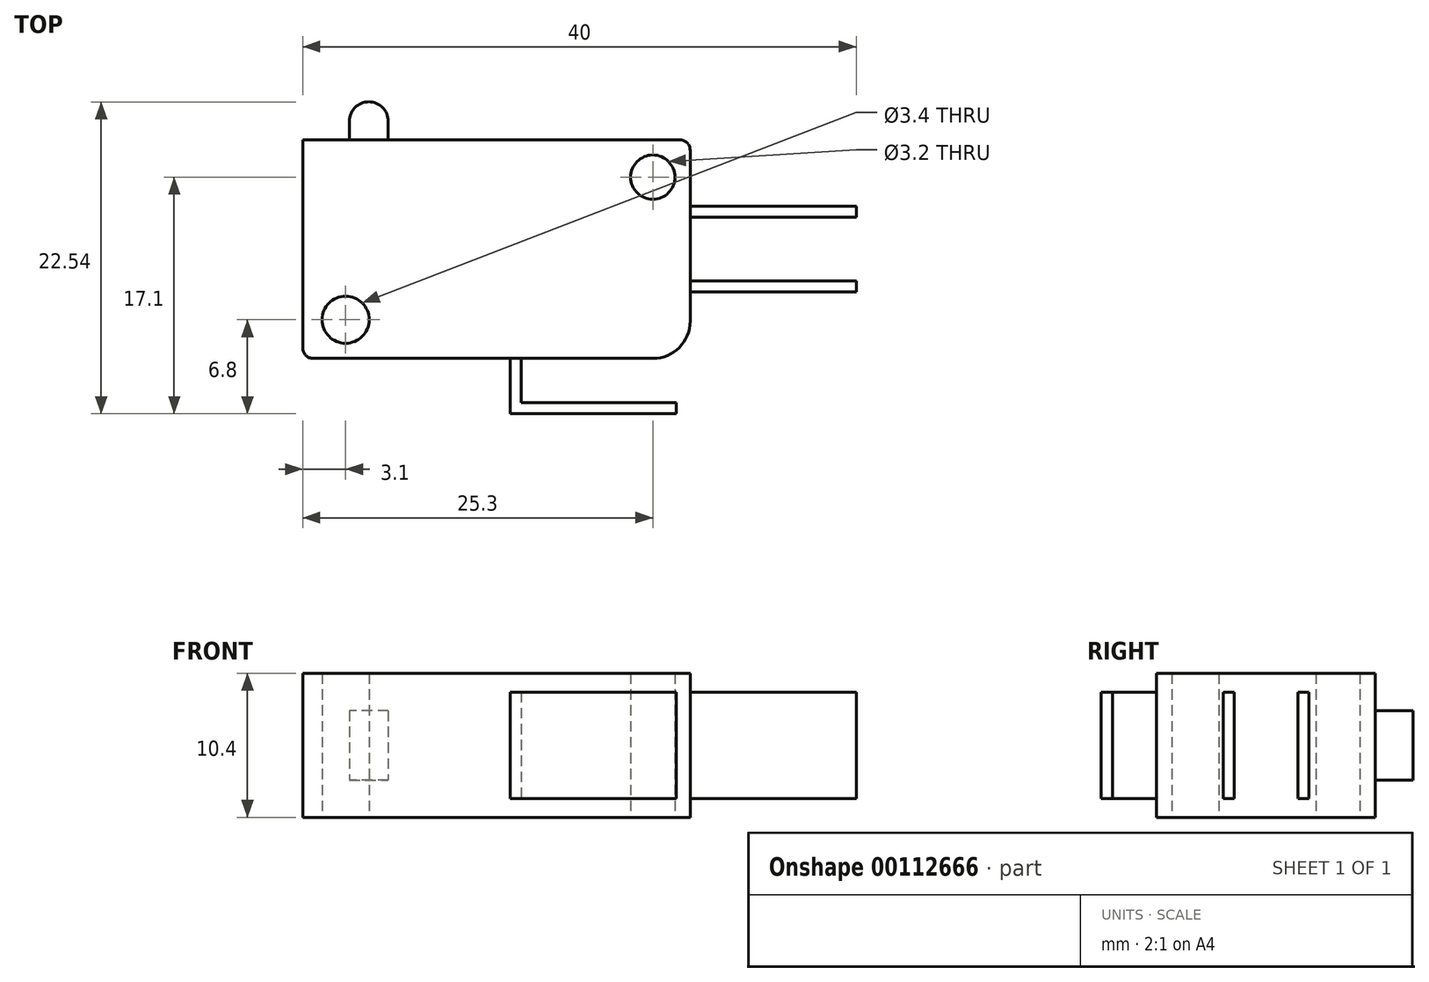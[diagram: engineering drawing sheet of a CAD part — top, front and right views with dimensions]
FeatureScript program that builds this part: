
annotation { "Feature Type Name" : "Feature", "Feature Type Description" : "" }
export const myFeature = defineFeature(function(context is Context, id is Id, definition is map)
    precondition{}
    {
        {
            var Q0;
            Q0=qCreatedBy(makeId("Top.planeOp"),FACE);
            var sketch = newSketch(context, id + "F0", { "sketchPlane" : qUnion([Q0])});
            skLineSegment(sketch, "E0.left", {"start": v(0, 0) * mm, "end": v(0, -15.8) * mm});
            skLineSegment(sketch, "E1", {"start": v(25.3, 0) * mm, "end": v(25.3, -2.7) * mm, "construction": true});
            skLineSegment(sketch, "E2", {"start": v(25.3, -2.7) * mm, "end": v(28, -2.7) * mm, "construction": true});
            skLineSegment(sketch, "E3", {"start": v(3.1, -15.8) * mm, "end": v(3.1, -13) * mm, "construction": true});
            skLineSegment(sketch, "E4", {"start": v(3.1, -13) * mm, "end": v(0, -13) * mm, "construction": true});
            skCircle(sketch, "E5", {"center": v(3.1, -13) * mm, "radius": 1.7 * mm});
            skCircle(sketch, "E6", {"center": v(25.3, -2.7) * mm, "radius": 1.6 * mm});
            skLineSegment(sketch, "E7", {"start": v(0, -15.8) * mm, "end": v(15, -15.8) * mm});
            skLineSegment(sketch, "E8", {"start": v(15, -15.8) * mm, "end": v(15, -19.8) * mm});
            skLineSegment(sketch, "E9", {"start": v(15, -15.8) * mm, "end": v(15.8, -15.8) * mm, "construction": true});
            skLineSegment(sketch, "E10", {"start": v(15.8, -15.8) * mm, "end": v(15.8, -19) * mm});
            skLineSegment(sketch, "E11", {"start": v(15.8, -19) * mm, "end": v(27, -19) * mm});
            skLineSegment(sketch, "E12", {"start": v(27, -19) * mm, "end": v(27, -19.8) * mm});
            skLineSegment(sketch, "E13", {"start": v(27, -19.8) * mm, "end": v(15, -19.8) * mm});
            skLineSegment(sketch, "E14", {"start": v(15.8, -15.8) * mm, "end": v(28, -15.8) * mm});
            skLineSegment(sketch, "E15", {"start": v(28, 0) * mm, "end": v(28, -4.8) * mm});
            skLineSegment(sketch, "E16", {"start": v(28, -15.8) * mm, "end": v(28, -11) * mm});
            skLineSegment(sketch, "E17.bottom", {"start": v(28, -4.8) * mm, "end": v(40, -4.8) * mm});
            skLineSegment(sketch, "E17.top", {"start": v(28, -5.6) * mm, "end": v(40, -5.6) * mm});
            skLineSegment(sketch, "E17.left", {"start": v(28, -4.8) * mm, "end": v(28, -5.6) * mm, "construction": true});
            skLineSegment(sketch, "E17.right", {"start": v(40, -4.8) * mm, "end": v(40, -5.6) * mm});
            skLineSegment(sketch, "E18.bottom", {"start": v(28, -11) * mm, "end": v(40, -11) * mm});
            skLineSegment(sketch, "E18.top", {"start": v(28, -10.2) * mm, "end": v(40, -10.2) * mm});
            skLineSegment(sketch, "E18.left", {"start": v(28, -11) * mm, "end": v(28, -10.2) * mm, "construction": true});
            skLineSegment(sketch, "E18.right", {"start": v(40, -11) * mm, "end": v(40, -10.2) * mm});
            skLineSegment(sketch, "E19", {"start": v(28, -10.2) * mm, "end": v(28, -5.6) * mm});
            skLineSegment(sketch, "E20", {"start": v(0, 0) * mm, "end": v(3.38, 0) * mm});
            skLineSegment(sketch, "E21.bottom", {"start": v(3.38, 0) * mm, "end": v(6.17, 0) * mm, "construction": true});
            skLineSegment(sketch, "E21.top", {"start": v(3.38, 1.35) * mm, "end": v(6.17, 1.35) * mm, "construction": true});
            skLineSegment(sketch, "E21.left", {"start": v(3.38, 0) * mm, "end": v(3.38, 1.35) * mm});
            skLineSegment(sketch, "E21.right", {"start": v(6.17, 0) * mm, "end": v(6.17, 1.35) * mm});
            skArc(sketch, "E22", {"start": v(6.17, 1.35) * mm, "mid": v(4.78, 2.74) * mm, "end": v(3.38, 1.35) * mm});
            skLineSegment(sketch, "E23", {"start": v(6.17, 0) * mm, "end": v(28, 0) * mm});
            skSolve(sketch);
        }
        {
            var Q0;
            Q0=makeQuery(id+"F0.imprint","IMPRINT",FACE,{"disambiguationData":[TD([[makeQuery(id+"F0.imprint","IMPRINT",EDGE,{"derivedFrom":sQuery(id+"F0.wireOp",EDGE,"E0.bottom")}),-1.0]])]});
            var Q1;
            Q1=makeQuery(id+"F0.imprint","IMPRINT",FACE,{"disambiguationData":[TD([[makeQuery(id+"F0.imprint","IMPRINT",EDGE,{"derivedFrom":sQuery(id+"F0.wireOp",EDGE,"E0.left")}),1.0]])]});
            extrude(context, id + "F1", {"entities" : qUnion([Q0, Q1]), "depth" : 10.4 * mm});
        }
        {
            var Q0;
            Q0=makeQuery(id+"F1.opExtrude","SWEPT_FACE",FACE,{"disambiguationData":[OSD([sQuery(id+"F0.wireOp",EDGE,"E0.left")])]});
            var sketch = newSketch(context, id + "F2", { "sketchPlane" : qUnion([Q0])});
            skLineSegment(sketch, "E24.bottom", {"start": v(0, 10.4) * mm, "end": v(-12.7, 10.4) * mm});
            skLineSegment(sketch, "E24.top", {"start": v(0, 7.7) * mm, "end": v(-12.7, 7.7) * mm});
            skLineSegment(sketch, "E24.left", {"start": v(0, 10.4) * mm, "end": v(0, 7.7) * mm});
            skLineSegment(sketch, "E24.right", {"start": v(-12.7, 10.4) * mm, "end": v(-12.7, 7.7) * mm});
            skLineSegment(sketch, "E25.bottom", {"start": v(-12.7, 0) * mm, "end": v(0, 0) * mm});
            skLineSegment(sketch, "E25.top", {"start": v(-12.7, 2.7) * mm, "end": v(0, 2.7) * mm});
            skLineSegment(sketch, "E25.left", {"start": v(-12.7, 0) * mm, "end": v(-12.7, 2.7) * mm});
            skLineSegment(sketch, "E25.right", {"start": v(0, 0) * mm, "end": v(0, 2.7) * mm});
            skLineSegment(sketch, "E26.bottom", {"start": v(15.8, 10.4) * mm, "end": v(19.8, 10.4) * mm});
            skLineSegment(sketch, "E26.top", {"start": v(15.8, 9.05) * mm, "end": v(19.8, 9.05) * mm});
            skLineSegment(sketch, "E26.left", {"start": v(15.8, 10.4) * mm, "end": v(15.8, 9.05) * mm});
            skLineSegment(sketch, "E26.right", {"start": v(19.8, 10.4) * mm, "end": v(19.8, 9.05) * mm});
            skLineSegment(sketch, "E27.bottom", {"start": v(15.8, 0) * mm, "end": v(19.8, 0) * mm});
            skLineSegment(sketch, "E27.top", {"start": v(15.8, 1.35) * mm, "end": v(19.8, 1.35) * mm});
            skLineSegment(sketch, "E27.left", {"start": v(15.8, 0) * mm, "end": v(15.8, 1.35) * mm});
            skLineSegment(sketch, "E27.right", {"start": v(19.8, 0) * mm, "end": v(19.8, 1.35) * mm});
            skSolve(sketch);
        }
        {
            var Q0;
            Q0 = qSketchRegion(id + "F2", true);
            var Q1;
            Q1=makeQuery(id+"F1.opExtrude","SWEPT_FACE",FACE,{"disambiguationData":[OSD([sQuery(id+"F0.wireOp",EDGE,"E15")])]});
            extrude(context, id + "F3", {"entities" : qUnion([Q0]), "operationType" : NewBodyOperationType.REMOVE, "endBound" : BoundingType.UP_TO_SURFACE, "oppositeDirection" : true, "endBoundEntityFace" : qUnion([Q1]), "depth" : 25.4 * mm});
        }
        {
            var Q0;
            Q0=makeQuery(id+"F1.opExtrude","SWEPT_FACE",FACE,{"disambiguationData":[OSD([sQuery(id+"F0.wireOp",EDGE,"E17.bottom")])]});
            var sketch = newSketch(context, id + "F4", { "sketchPlane" : qUnion([Q0])});
            skLineSegment(sketch, "E28.bottom", {"start": v(-28, 10.4) * mm, "end": v(-40, 10.4) * mm});
            skLineSegment(sketch, "E28.top", {"start": v(-28, 9.05) * mm, "end": v(-40, 9.05) * mm});
            skLineSegment(sketch, "E28.left", {"start": v(-28, 10.4) * mm, "end": v(-28, 9.05) * mm});
            skLineSegment(sketch, "E28.right", {"start": v(-40, 10.4) * mm, "end": v(-40, 9.05) * mm});
            skLineSegment(sketch, "E29.bottom", {"start": v(-40, 0) * mm, "end": v(-28, 0) * mm});
            skLineSegment(sketch, "E29.top", {"start": v(-40, 1.35) * mm, "end": v(-28, 1.35) * mm});
            skLineSegment(sketch, "E29.left", {"start": v(-40, 0) * mm, "end": v(-40, 1.35) * mm});
            skLineSegment(sketch, "E29.right", {"start": v(-28, 0) * mm, "end": v(-28, 1.35) * mm});
            skSolve(sketch);
        }
        {
            var Q0;
            Q0 = qSketchRegion(id + "F4", true);
            var Q1;
            Q1=makeQuery(id+"F1.opExtrude","SWEPT_FACE",FACE,{"disambiguationData":[OSD([sQuery(id+"F0.wireOp",EDGE,"E18.bottom")])]});
            extrude(context, id + "F5", {"entities" : qUnion([Q0]), "operationType" : NewBodyOperationType.REMOVE, "endBound" : BoundingType.UP_TO_SURFACE, "oppositeDirection" : true, "endBoundEntityFace" : qUnion([Q1]), "depth" : 25.4 * mm});
        }
        {
            var Q0;
            Q0=makeQuery(id+"F1.opExtrude","SWEPT_EDGE",EDGE,{"disambiguationData":[OSD([sQuery(id+"F0.wireOp",EDGE,"E14"),sQuery(id+"F0.wireOp",EDGE,"E16")])]});
            var Q1;
            Q1=makeQuery(id+"F3.boolean.opBoolean","INTERSECT",EDGE,{"derivedFrom":[makeQuery(id+"F3.opExtrude","SWEPT_FACE",FACE,{"disambiguationData":[OSD([sQuery(id+"F2.wireOp",EDGE,"E24.left")])]}),makeQuery(id+"F3.opExtrude","SWEPT_FACE",FACE,{"disambiguationData":[OSD([sQuery(id+"F2.wireOp",EDGE,"E25.right")])]})]});
            fillet(context, id + "F6", {"entities" : qUnion([Q0, Q1]), "radius" : 2.7 * mm, "tangentPropagation" : true, "allowEdgeOverflow" : false});
        }
        {
            var Q0;
            Q0=makeQuery(id+"F1.opExtrude","SWEPT_EDGE",EDGE,{"disambiguationData":[OSD([sQuery(id+"F0.wireOp",EDGE,"E15"),sQuery(id+"F0.wireOp",EDGE,"E23")])]});
            var Q1;
            Q1=makeQuery(id+"F1.opExtrude","SWEPT_EDGE",EDGE,{"disambiguationData":[OSD([sQuery(id+"F0.wireOp",EDGE,"E0.left"),sQuery(id+"F0.wireOp",EDGE,"E7")])]});
            fillet(context, id + "F7", {"entities" : qUnion([Q0, Q1]), "radius" : 0.76 * mm, "tangentPropagation" : true, "allowEdgeOverflow" : false});
        }
    });
